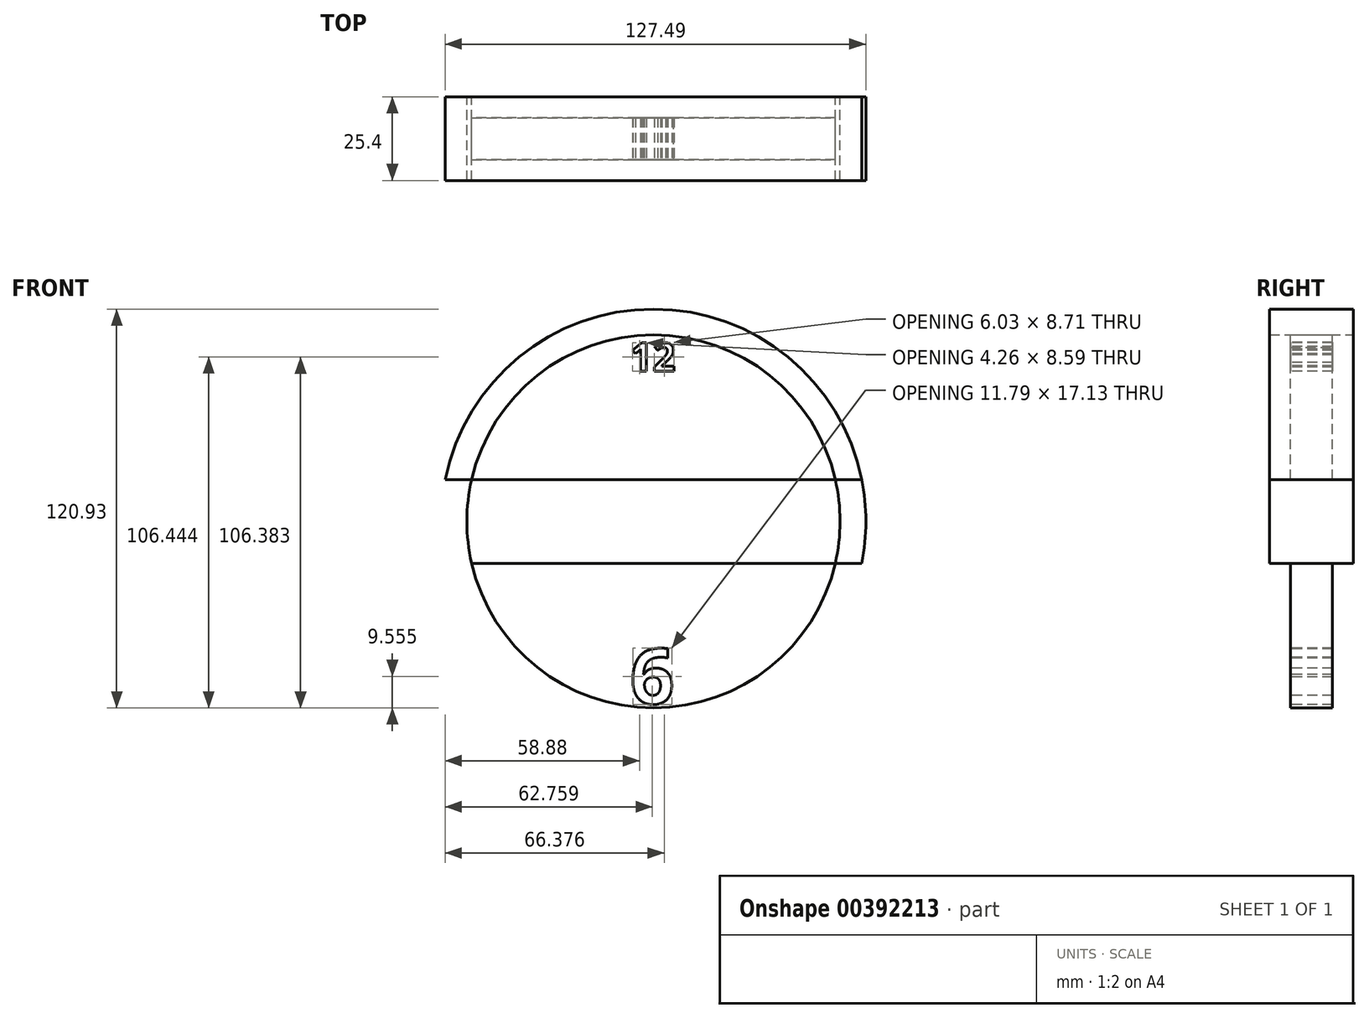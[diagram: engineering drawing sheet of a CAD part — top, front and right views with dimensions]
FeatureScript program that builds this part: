
annotation { "Feature Type Name" : "Feature", "Feature Type Description" : "" }
export const myFeature = defineFeature(function(context is Context, id is Id, definition is map)
    precondition{}
    {
        {
            var Q0;
            Q0=qCreatedBy(makeId("Front.planeOp"),FACE);
            var sketch = newSketch(context, id + "F0", { "sketchPlane" : qUnion([Q0])});
            skCircle(sketch, "E0", {"center": v(0, 0) * mm, "radius": 64.38 * mm});
            skLineSegment(sketch, "E1", {"start": v(-63.11, 12.7) * mm, "end": v(63.11, 12.7) * mm});
            skLineSegment(sketch, "E2", {"start": v(-63.11, -12.7) * mm, "end": v(63.11, -12.7) * mm});
            skCircle(sketch, "E3", {"center": v(0, 0) * mm, "radius": 56.55 * mm});
            skSolve(sketch);
        }
        {
            var Q0;
            {var subQ0=sQuery(id+"F0.wireOp",EDGE,"E1");var subQ1=sQuery(id+"F0.wireOp",EDGE,"E0");var subQ2=makeQuery(id+"F0.imprint","INTERSECT",VERTEX,{"disambiguationData":[OD(0.0)],"derivedFrom":[subQ1,subQ0]});Q0=makeQuery(id+"F0.imprint","IMPRINT",FACE,{"disambiguationData":[TD([[makeQuery(id+"F0.imprint","IMPRINT",EDGE,{"disambiguationData":[TD([[subQ2,1.0]])],"derivedFrom":subQ1}),1.0]])]});}
            extrude(context, id + "F1", {"entities" : qUnion([Q0]), "endBound" : BoundingType.SYMMETRIC, "depth" : 25.4 * mm});
        }
        {
            var Q0;
            {var subQ0=sQuery(id+"F0.wireOp",EDGE,"E3");var subQ1=sQuery(id+"F0.wireOp",EDGE,"E1");var subQ2=makeQuery(id+"F0.imprint","INTERSECT",VERTEX,{"disambiguationData":[OD(0.0)],"derivedFrom":[subQ1,subQ0]});Q0=makeQuery(id+"F0.imprint","IMPRINT",FACE,{"disambiguationData":[TD([[makeQuery(id+"F0.imprint","IMPRINT",EDGE,{"disambiguationData":[TD([[subQ2,-1.0]])],"derivedFrom":subQ1}),-1.0]])]});}
            extrude(context, id + "F2", {"entities" : qUnion([Q0]), "endBound" : BoundingType.SYMMETRIC, "depth" : 25.4 * mm});
        }
        {
            var Q0;
            {var subQ0=sQuery(id+"F0.wireOp",EDGE,"E1");var subQ1=sQuery(id+"F0.wireOp",EDGE,"E0");var subQ2=makeQuery(id+"F0.imprint","INTERSECT",VERTEX,{"disambiguationData":[OD(0.0)],"derivedFrom":[subQ1,subQ0]});Q0=makeQuery(id+"F0.imprint","IMPRINT",FACE,{"disambiguationData":[TD([[makeQuery(id+"F0.imprint","IMPRINT",EDGE,{"disambiguationData":[TD([[subQ2,-1.0]])],"derivedFrom":subQ1}),1.0]])]});}
            var Q1;
            {var subQ0=sQuery(id+"F0.wireOp",EDGE,"E1");var subQ1=sQuery(id+"F0.wireOp",EDGE,"E0");var subQ2=makeQuery(id+"F0.imprint","INTERSECT",VERTEX,{"disambiguationData":[OD(1.0)],"derivedFrom":[subQ1,subQ0]});Q1=makeQuery(id+"F0.imprint","IMPRINT",FACE,{"disambiguationData":[TD([[makeQuery(id+"F0.imprint","IMPRINT",EDGE,{"disambiguationData":[TD([[subQ2,1.0]])],"derivedFrom":subQ1}),1.0]])]});}
            extrude(context, id + "F3", {"entities" : qUnion([Q0, Q1]), "endBound" : BoundingType.SYMMETRIC, "depth" : 25.4 * mm});
        }
        {
            var Q0;
            {var subQ0=sQuery(id+"F0.wireOp",EDGE,"E2");var subQ1=sQuery(id+"F0.wireOp",EDGE,"E0");var subQ2=makeQuery(id+"F0.imprint","INTERSECT",VERTEX,{"disambiguationData":[OD(0.0)],"derivedFrom":[subQ1,subQ0]});Q0=makeQuery(id+"F0.imprint","IMPRINT",FACE,{"disambiguationData":[TD([[makeQuery(id+"F0.imprint","IMPRINT",EDGE,{"disambiguationData":[TD([[subQ2,-1.0]])],"derivedFrom":subQ1}),1.0]])]});}
            extrude(context, id + "F4", {"entities" : qUnion([Q0]), "endBound" : BoundingType.SYMMETRIC, "depth" : 25.4 * mm});
        }
        {
            var Q0;
            {var subQ0=sQuery(id+"F0.wireOp",EDGE,"E3");var subQ1=sQuery(id+"F0.wireOp",EDGE,"E1");var subQ2=makeQuery(id+"F0.imprint","INTERSECT",VERTEX,{"disambiguationData":[OD(0.0)],"derivedFrom":[subQ1,subQ0]});Q0=makeQuery(id+"F0.imprint","IMPRINT",FACE,{"disambiguationData":[TD([[makeQuery(id+"F0.imprint","IMPRINT",EDGE,{"disambiguationData":[TD([[subQ2,-1.0]])],"derivedFrom":subQ1}),1.0]])]});}
            var Q1;
            {var subQ0=sQuery(id+"F0.wireOp",EDGE,"E3");var subQ1=sQuery(id+"F0.wireOp",EDGE,"E2");var subQ2=makeQuery(id+"F0.imprint","INTERSECT",VERTEX,{"disambiguationData":[OD(0.0)],"derivedFrom":[subQ1,subQ0]});Q1=makeQuery(id+"F0.imprint","IMPRINT",FACE,{"disambiguationData":[TD([[makeQuery(id+"F0.imprint","IMPRINT",EDGE,{"disambiguationData":[TD([[subQ2,-1.0]])],"derivedFrom":subQ1}),-1.0]])]});}
            extrude(context, id + "F5", {"entities" : qUnion([Q0, Q1]), "endBound" : BoundingType.SYMMETRIC, "depth" : 12.7 * mm});
        }
        {
            var Q0;
            Q0=qCreatedBy(makeId("Front.planeOp"),FACE);
            var sketch = newSketch(context, id + "F6", { "sketchPlane" : qUnion([Q0])});
            skText(sketch, "E4", { "text": "12", "fontName": "OpenSans-Bold.ttf"});
            skText(sketch, "E5", { "text": "12", "fontName": "OpenSans-Bold.ttf"});
            skText(sketch, "E6", { "text": "12", "fontName": "OpenSans-Bold.ttf"});
            skText(sketch, "E7", { "text": "12", "fontName": "OpenSans-Bold.ttf"});
            skText(sketch, "E8", { "text": "6", "fontName": "OpenSans-Bold.ttf"});
            const initialGuessF6  = {"E4": [-0.00707, 0.04554, 1, 0, 0.00866], "E5": [-0.00357, 0.09605, 1, 0, 0.00866], "E6": [-0.03438, 0.10213, 1, 0, 0.00866], "E7": [-0.03087, 0.15265, 1, 0, 0.00866], "E8": [-0.00707, -0.05533, 1, 0, 0.01685]};
            skSetInitialGuess(sketch, initialGuessF6);
            skSolve(sketch);
        }
        {
            var Q0;
            Q0 = qSketchRegion(id + "F6", true);
            extrude(context, id + "F7", {"entities" : qUnion([Q0]), "operationType" : NewBodyOperationType.REMOVE, "endBound" : BoundingType.SYMMETRIC, "oppositeDirection" : true, "depth" : 12.7 * mm});
        }
    });
